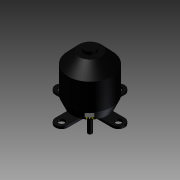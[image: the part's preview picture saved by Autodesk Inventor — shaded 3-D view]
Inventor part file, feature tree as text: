
AUTODESK INVENTOR PART (.ipt)
format: ipt  version: 2011 SP1 (Build 150282100, 282)  size: 199,168 bytes
history: native  units: in
note: dims shown in document units (in); Inventor stores cm internally (conversion verified against a paired STEP export)
features: sketch x7, extrude x3, revolve x1, plane x1
ambient origin geometry x8: Origin, YZ Plane, XZ Plane, XY Plane, X Axis, Y Axis, Z Axis, Center Point
bodies: Solid1 (feature_tree)
feature tree (12):
  revolve  "Revolution1"  [1 undecoded]
  extrude  "Extrusion1"  Depth=0.672in
  plane  "Work Plane1"
  extrude  "Extrusion2"  Depth=0.1075in
  extrude  "Extrusion3"  Depth=0.0385in
  sketch  "Sketch5"  dims[d9=0.2075in]
  sketch  "Sketch6"  dims[d10=0.337in]
  sketch  "Sketch7"  dims[d14=90.0deg d15=0.237in d16=0.125in d17=0.1185in d18=0.535in d19=0.535in d20=0.535in d21=0.323in d22=0.118in d23=0.043in d24=0.0in d25=0.0625in d26=0.01in d27=0.0in d28=0.0in d29=0.01in d30=0.0in]
  sketch  "Sketch1"  dims[d0=0.945in d1=0.414in]
  sketch  "Sketch2"  dims[d2=0.888in d3=0.672in]
  sketch  "Sketch3"  dims[d4=0.171in d5=0.1075in]
  sketch  "Sketch4"  dims[d6=0.456in d7=0.0385in]
note: 1 required parameter value undecoded (feature->parameter linkage not recoverable at this tier; creation-order binding heuristic only, values carry confidence <= 0.55)
